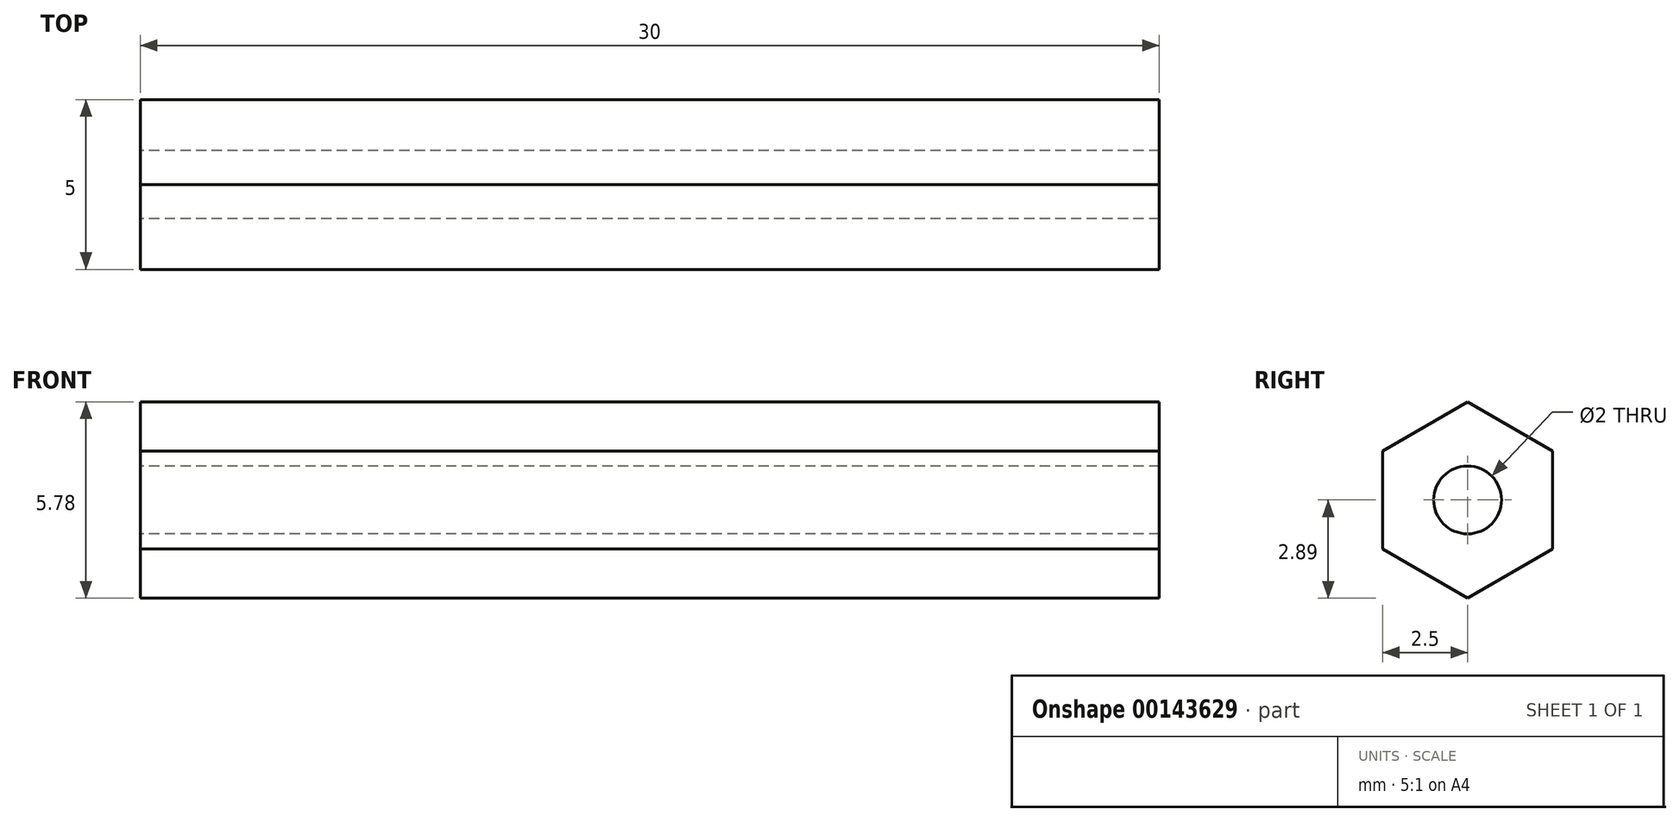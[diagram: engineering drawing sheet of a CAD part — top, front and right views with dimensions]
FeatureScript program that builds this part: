
annotation { "Feature Type Name" : "Feature", "Feature Type Description" : "" }
export const myFeature = defineFeature(function(context is Context, id is Id, definition is map)
    precondition{}
    {
        {
            var Q0;
            Q0=qCreatedBy(makeId("Right.planeOp"),FACE);
            var sketch = newSketch(context, id + "F0", { "sketchPlane" : qUnion([Q0])});
            skCircle(sketch, "E0.cCircle", {"center": v(0, 0) * mm, "radius": 2.5 * mm, "construction": true});
            skLineSegment(sketch, "E0.0", {"start": v(2.5, 1.44) * mm, "end": v(2.5, -1.44) * mm});
            skLineSegment(sketch, "E0.1", {"start": v(2.5, -1.44) * mm, "end": v(0, -2.89) * mm});
            skLineSegment(sketch, "E0.2", {"start": v(0, -2.89) * mm, "end": v(-2.5, -1.44) * mm});
            skLineSegment(sketch, "E0.3", {"start": v(-2.5, -1.44) * mm, "end": v(-2.5, 1.44) * mm});
            skLineSegment(sketch, "E0.4", {"start": v(-2.5, 1.44) * mm, "end": v(0, 2.89) * mm});
            skLineSegment(sketch, "E0.5", {"start": v(0, 2.89) * mm, "end": v(2.5, 1.44) * mm});
            skPoint(sketch, "E0.0.midPoint", {"position": v(2.5, 0) * mm});
            skCircle(sketch, "E1", {"center": v(0, 0) * mm, "radius": 1 * mm});
            skSolve(sketch);
        }
        {
            var Q0;
            Q0 = qSketchRegion(id + "F0", true);
            extrude(context, id + "F1", {"entities" : qUnion([Q0]), "flatOperationType" : FlatOperationType.REMOVE, "offsetDistance" : 25 * mm, "depth" : 30 * mm, "domain" : OperationDomain.MODEL});
        }
    });
